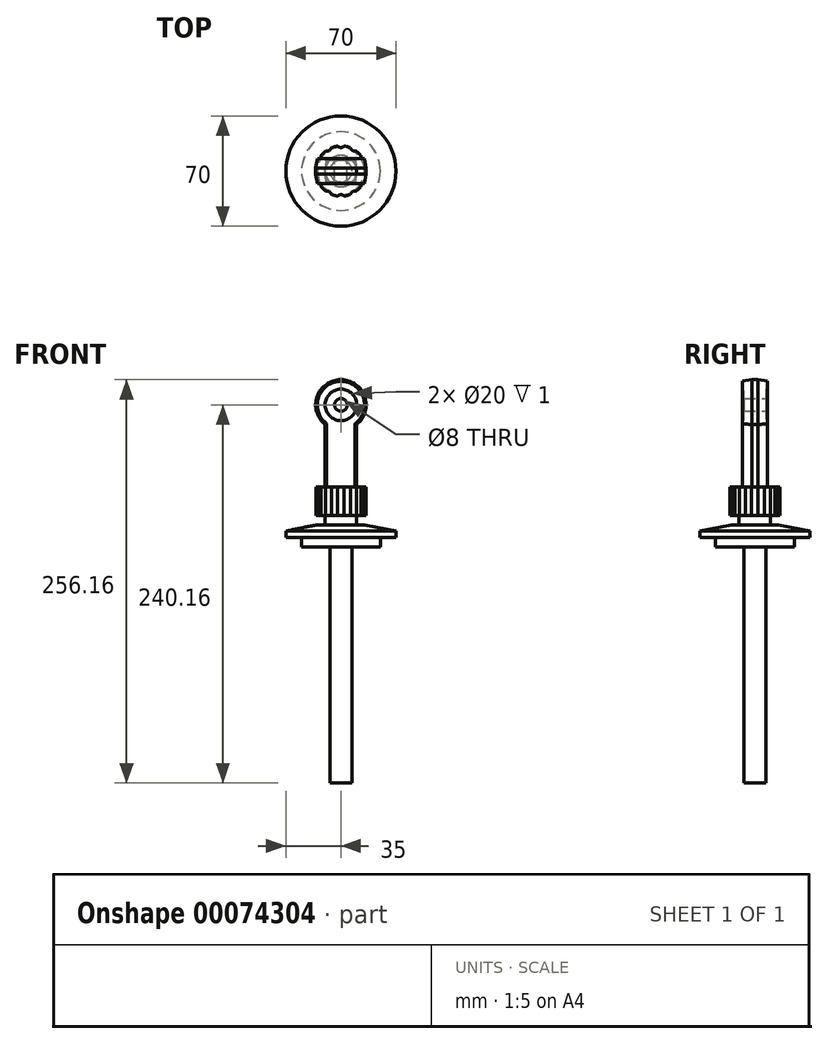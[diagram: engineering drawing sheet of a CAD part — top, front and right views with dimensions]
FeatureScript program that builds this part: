
annotation { "Feature Type Name" : "Feature", "Feature Type Description" : "" }
export const myFeature = defineFeature(function(context is Context, id is Id, definition is map)
    precondition{}
    {
        {
            var Q0;
            Q0=qCreatedBy(makeId("Front.planeOp"),FACE);
            var sketch = newSketch(context, id + "F0", { "sketchPlane" : qUnion([Q0])});
            skArc(sketch, "E0", {"start": v(10, -12.49) * mm, "mid": v(0, 16) * mm, "end": v(-10, -12.49) * mm});
            skLineSegment(sketch, "E1", {"start": v(0, 0) * mm, "end": v(0, -51.95) * mm, "construction": true});
            skLineSegment(sketch, "E2", {"start": v(-10, -12.49) * mm, "end": v(-10, -52.16) * mm});
            skLineSegment(sketch, "E3", {"start": v(10, -12.49) * mm, "end": v(10, -52.16) * mm});
            skLineSegment(sketch, "E4", {"start": v(-10, -52.16) * mm, "end": v(10, -52.16) * mm});
            skPoint(sketch, "E5.orphan", {"position": v(10, -53.63) * mm});
            skCircle(sketch, "E6", {"center": v(0, 0) * mm, "radius": 4 * mm});
            skSolve(sketch);
        }
        {
            var Q0;
            Q0 = qSketchRegion(id + "F0", true);
            extrude(context, id + "F1", {"entities" : qUnion([Q0]), "depth" : 16 * mm, "symmetric" : true});
        }
        {
            var Q0;
            Q0=makeQuery(id+"F1.opExtrude","CAP_FACE",FACE,{"disambiguationData":[OSD([sQuery(id+"F0.wireOp",EDGE,"E0"),sQuery(id+"F0.wireOp",EDGE,"E2"),sQuery(id+"F0.wireOp",EDGE,"E3"),sQuery(id+"F0.wireOp",EDGE,"E4"),sQuery(id+"F0.wireOp",EDGE,"E6")])],"isStart":false});
            var sketch = newSketch(context, id + "F2", { "sketchPlane" : qUnion([Q0])});
            skCircle(sketch, "E7", {"center": v(0, 0) * mm, "radius": 10 * mm});
            skSolve(sketch);
        }
        {
            var Q0;
            Q0 = qSketchRegion(id + "F2", true);
            extrude(context, id + "F3", {"entities" : qUnion([Q0]), "operationType" : NewBodyOperationType.REMOVE, "oppositeDirection" : true, "depth" : 1 * mm});
        }
        {
            var Q0;
            Q0=makeQuery(id+"F1.opExtrude","CAP_FACE",FACE,{"disambiguationData":[OSD([sQuery(id+"F0.wireOp",EDGE,"E0"),sQuery(id+"F0.wireOp",EDGE,"E2"),sQuery(id+"F0.wireOp",EDGE,"E3"),sQuery(id+"F0.wireOp",EDGE,"E4"),sQuery(id+"F0.wireOp",EDGE,"E6")])],"isStart":true});
            var sketch = newSketch(context, id + "F4", { "sketchPlane" : qUnion([Q0])});
            skCircle(sketch, "E8", {"center": v(0, 0) * mm, "radius": 10 * mm});
            skSolve(sketch);
        }
        {
            var Q0;
            Q0 = qSketchRegion(id + "F4", true);
            extrude(context, id + "F5", {"entities" : qUnion([Q0]), "operationType" : NewBodyOperationType.REMOVE, "oppositeDirection" : true, "depth" : 1 * mm});
        }
        {
            var Q0;
            Q0=makeQuery(id+"F1.opExtrude","CAP_EDGE",EDGE,{"disambiguationData":[OSD([sQuery(id+"F0.wireOp",EDGE,"E0")])],"isStart":true});
            var Q1;
            Q1=makeQuery(id+"F1.opExtrude","CAP_EDGE",EDGE,{"disambiguationData":[OSD([sQuery(id+"F0.wireOp",EDGE,"E3")])],"isStart":true});
            var Q2;
            Q2=makeQuery(id+"F1.opExtrude","CAP_EDGE",EDGE,{"disambiguationData":[OSD([sQuery(id+"F0.wireOp",EDGE,"E2")])],"isStart":true});
            chamfer(context, id + "F6", {"entities" : qUnion([Q0, Q1, Q2]), "chamferType" : ChamferType.TWO_OFFSETS, "width1" : 6 * mm, "oppositeDirection" : false, "width2" : 1 * mm, "tangentPropagation" : true});
        }
        {
            var Q0;
            Q0=makeQuery(id+"F1.opExtrude","CAP_EDGE",EDGE,{"disambiguationData":[OSD([sQuery(id+"F0.wireOp",EDGE,"E0")])],"isStart":false});
            var Q1;
            Q1=makeQuery(id+"F1.opExtrude","CAP_EDGE",EDGE,{"disambiguationData":[OSD([sQuery(id+"F0.wireOp",EDGE,"E2")])],"isStart":false});
            var Q2;
            Q2=makeQuery(id+"F1.opExtrude","CAP_EDGE",EDGE,{"disambiguationData":[OSD([sQuery(id+"F0.wireOp",EDGE,"E3")])],"isStart":false});
            chamfer(context, id + "F7", {"entities" : qUnion([Q0, Q1, Q2]), "chamferType" : ChamferType.TWO_OFFSETS, "width1" : 1 * mm, "oppositeDirection" : false, "width2" : 6 * mm, "tangentPropagation" : true});
        }
        {
            var Q0;
            Q0=makeQuery(id+"F1.opExtrude","SWEPT_FACE",FACE,{"disambiguationData":[OSD([sQuery(id+"F0.wireOp",EDGE,"E4")])]});
            var sketch = newSketch(context, id + "F8", { "sketchPlane" : qUnion([Q0])});
            skCircle(sketch, "E9", {"center": v(0, 0) * mm, "radius": 16 * mm});
            skSolve(sketch);
        }
        {
            var Q0;
            Q0 = qSketchRegion(id + "F8", true);
            extrude(context, id + "F9", {"entities" : qUnion([Q0]), "operationType" : NewBodyOperationType.ADD, "depth" : 18 * mm});
        }
        {
            var Q0;
            Q0=makeQuery(id+"F9.opExtrude","CAP_FACE",FACE,{"disambiguationData":[OSD([sQuery(id+"F8.wireOp",EDGE,"E9")])],"isStart":false});
            var sketch = newSketch(context, id + "F10", { "sketchPlane" : qUnion([Q0])});
            skCircle(sketch, "E10", {"center": v(-18.01, 0) * mm, "radius": 3 * mm});
            skSolve(sketch);
        }
        {
            var Q0;
            {var subQ0=sQuery(id+"F10.wireOp",EDGE,"E10");var subQ1=makeQuery(id+"F9.opExtrude","CAP_EDGE",EDGE,{"disambiguationData":[OSD([sQuery(id+"F8.wireOp",EDGE,"E9")])],"isStart":false});var subQ2=makeQuery(id+"F10.imprint","INTERSECT",VERTEX,{"disambiguationData":[OD(0.0)],"derivedFrom":[subQ1,subQ0]});Q0=makeQuery(id+"F10.imprint","IMPRINT",FACE,{"disambiguationData":[TD([[makeQuery(id+"F10.imprint","IMPRINT",EDGE,{"disambiguationData":[TD([[subQ2,1.0]])],"derivedFrom":subQ0}),1.0]])]});}
            var Q1;
            Q1=sQuery(id+"F10.wireOp",EDGE,"E10");
            extrude(context, id + "F11", {"entities" : qUnion([Q0]), "operationType" : NewBodyOperationType.REMOVE, "surfaceEntities" : qUnion([Q1]), "oppositeDirection" : true, "depth" : 25 * mm});
        }
        {
            var Q0;
            Q0=makeQuery(id+"F11.boolean.opBoolean","COPY",FACE,{"derivedFrom":makeQuery(id+"F11.opExtrude","SWEPT_FACE",FACE,{"disambiguationData":[OSD([sQuery(id+"F10.wireOp",EDGE,"E10")])]})});
            var Q1;
            Q1=makeQuery(id+"F9.opExtrude","SWEPT_FACE",FACE,{"disambiguationData":[OSD([sQuery(id+"F8.wireOp",EDGE,"E9")])]});
            circularPattern(context, id + "F12", {"patternType" : PatternType.FACE, "faces" : qUnion([Q0]), "axis" : qUnion([Q1]), "angle" : 360 * degree, "instanceCount" : 12, "equalSpace" : true});
        }
        {
            var Q0;
            Q0=makeQuery(id+"F9.opExtrude","CAP_FACE",FACE,{"disambiguationData":[OSD([sQuery(id+"F8.wireOp",EDGE,"E9")])],"isStart":false});
            var sketch = newSketch(context, id + "F13", { "sketchPlane" : qUnion([Q0])});
            skCircle(sketch, "E11", {"center": v(0, 0) * mm, "radius": 10 * mm});
            skSolve(sketch);
        }
        {
            var Q0;
            Q0 = qSketchRegion(id + "F13", true);
            extrude(context, id + "F14", {"entities" : qUnion([Q0]), "operationType" : NewBodyOperationType.ADD, "depth" : 6 * mm});
        }
        {
            var Q0;
            Q0=makeQuery(id+"F14.opExtrude","CAP_FACE",FACE,{"disambiguationData":[OSD([sQuery(id+"F13.wireOp",EDGE,"E11")])],"isStart":false});
            var sketch = newSketch(context, id + "F15", { "sketchPlane" : qUnion([Q0])});
            skCircle(sketch, "E12", {"center": v(0, 0) * mm, "radius": 35 * mm});
            skSolve(sketch);
        }
        {
            var Q0;
            Q0 = qSketchRegion(id + "F15", true);
            extrude(context, id + "F16", {"entities" : qUnion([Q0]), "operationType" : NewBodyOperationType.ADD, "depth" : 8 * mm});
        }
        {
            var Q0;
            Q0=makeQuery(id+"F16.opExtrude","CAP_EDGE",EDGE,{"disambiguationData":[OSD([sQuery(id+"F15.wireOp",EDGE,"E12")])],"isStart":true});
            chamfer(context, id + "F17", {"entities" : qUnion([Q0]), "chamferType" : ChamferType.TWO_OFFSETS, "width1" : 4 * mm, "oppositeDirection" : false, "width2" : 20 * mm, "tangentPropagation" : true});
        }
        {
            var Q0;
            Q0=makeQuery(id+"F16.opExtrude","CAP_FACE",FACE,{"disambiguationData":[OSD([sQuery(id+"F15.wireOp",EDGE,"E12")])],"isStart":false});
            var sketch = newSketch(context, id + "F18", { "sketchPlane" : qUnion([Q0])});
            skCircle(sketch, "E13", {"center": v(0, 0) * mm, "radius": 25 * mm});
            skSolve(sketch);
        }
        {
            var Q0;
            Q0=makeQuery(id+"F18.imprint","IMPRINT",FACE,{"disambiguationData":[TD([[makeQuery(id+"F18.imprint","IMPRINT",EDGE,{"derivedFrom":sQuery(id+"F18.wireOp",EDGE,"E13")}),1.0]])]});
            extrude(context, id + "F19", {"entities" : qUnion([Q0]), "operationType" : NewBodyOperationType.ADD, "depth" : 6 * mm});
        }
        {
            var Q0;
            Q0=makeQuery(id+"F19.opExtrude","CAP_FACE",FACE,{"disambiguationData":[OSD([sQuery(id+"F18.wireOp",EDGE,"E13")])],"isStart":false});
            var sketch = newSketch(context, id + "F20", { "sketchPlane" : qUnion([Q0])});
            skCircle(sketch, "E14", {"center": v(0, 0) * mm, "radius": 7 * mm});
            skSolve(sketch);
        }
        {
            var Q0;
            Q0 = qSketchRegion(id + "F20", true);
            extrude(context, id + "F21", {"entities" : qUnion([Q0]), "operationType" : NewBodyOperationType.ADD, "depth" : 150 * mm});
        }
    });
